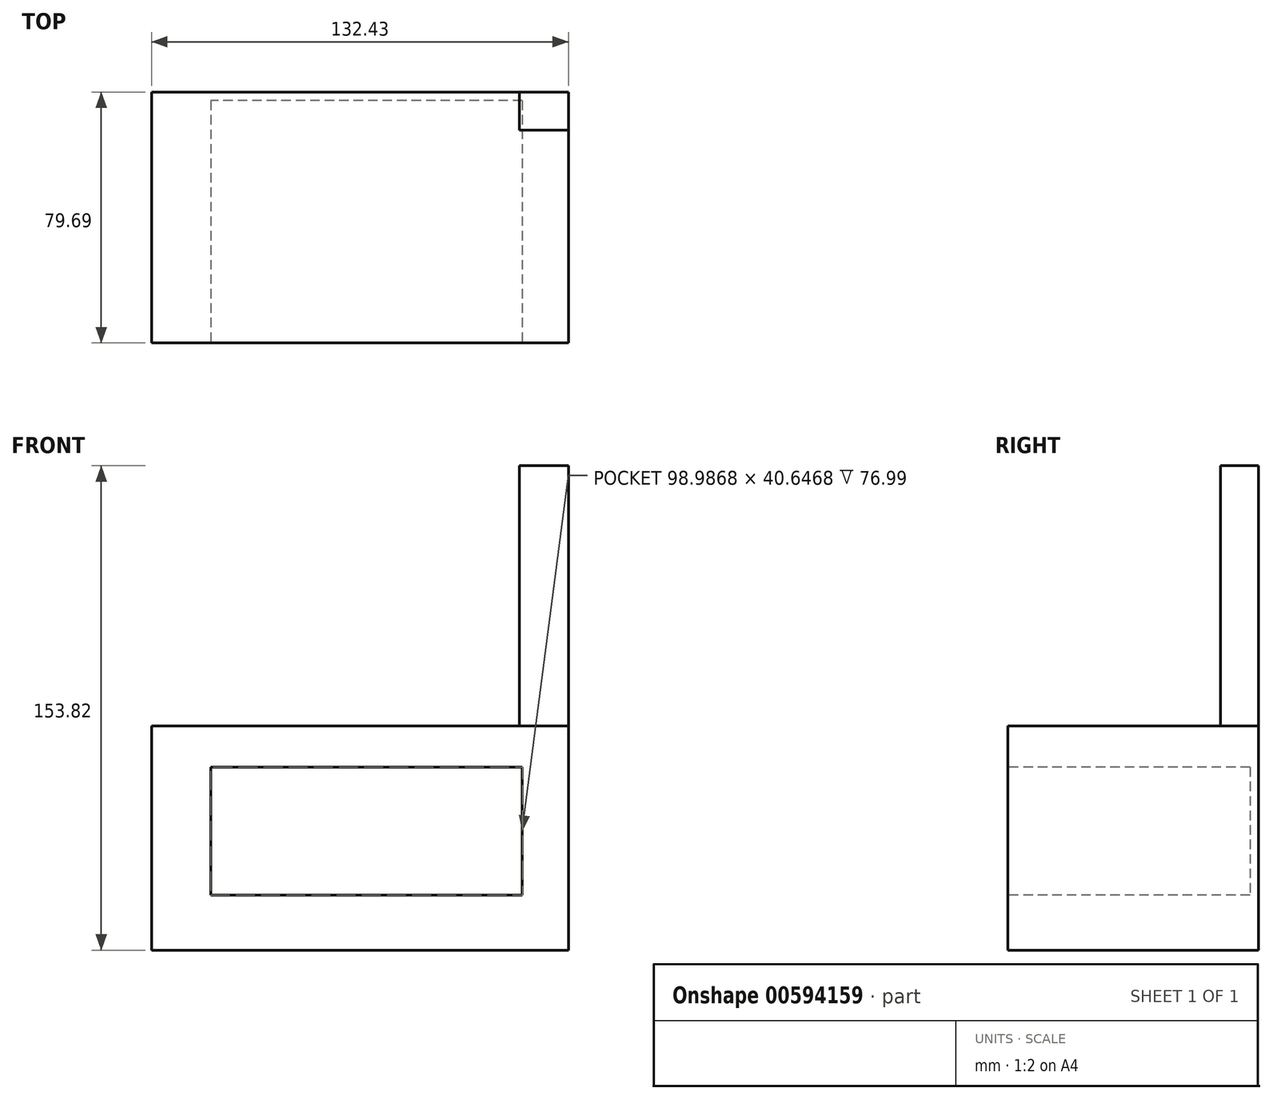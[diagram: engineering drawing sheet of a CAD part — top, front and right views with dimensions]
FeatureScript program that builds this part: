
annotation { "Feature Type Name" : "Feature", "Feature Type Description" : "" }
export const myFeature = defineFeature(function(context is Context, id is Id, definition is map)
    precondition{}
    {
        {
            var Q0;
            Q0=qCreatedBy(makeId("Top.planeOp"),FACE);
            var sketch = newSketch(context, id + "F0", { "sketchPlane" : qUnion([Q0])});
            skLineSegment(sketch, "E0.bottom", {"start": v(-68.33, -39.76) * mm, "end": v(64.1, -39.76) * mm});
            skLineSegment(sketch, "E0.top", {"start": v(-68.33, 39.93) * mm, "end": v(64.1, 39.93) * mm});
            skLineSegment(sketch, "E0.left", {"start": v(-68.33, -39.76) * mm, "end": v(-68.33, 39.93) * mm});
            skLineSegment(sketch, "E0.right", {"start": v(64.1, -39.76) * mm, "end": v(64.1, 39.93) * mm});
            skPoint(sketch, "E0.middle", {"position": v(-2.11, 0.09) * mm});
            skSolve(sketch);
        }
        {
            var Q0;
            Q0=makeQuery(id+"F0.imprint","IMPRINT",FACE,{"disambiguationData":[TD([[makeQuery(id+"F0.imprint","IMPRINT",EDGE,{"derivedFrom":sQuery(id+"F0.wireOp",EDGE,"E0.bottom")}),1.0]])]});
            extrude(context, id + "F1", {"entities" : qUnion([Q0]), "depth" : 71.13 * mm, "offsetDistance" : 25.4 * mm});
        }
        {
            var Q0;
            Q0=makeQuery(id+"F1.opExtrude","SWEPT_FACE",FACE,{"disambiguationData":[OSD([sQuery(id+"F0.wireOp",EDGE,"E0.bottom")])]});
            var sketch = newSketch(context, id + "F2", { "sketchPlane" : qUnion([Q0])});
            skLineSegment(sketch, "E1.bottom", {"start": v(49.5, 58.09) * mm, "end": v(-49.5, 58.09) * mm});
            skLineSegment(sketch, "E1.top", {"start": v(49.5, 17.44) * mm, "end": v(-49.5, 17.44) * mm});
            skLineSegment(sketch, "E1.left", {"start": v(49.5, 58.09) * mm, "end": v(49.5, 17.44) * mm});
            skLineSegment(sketch, "E1.right", {"start": v(-49.5, 58.09) * mm, "end": v(-49.5, 17.44) * mm});
            skPoint(sketch, "E1.middle", {"position": v(0, 37.76) * mm});
            skSolve(sketch);
        }
        {
            var Q0;
            Q0=makeQuery(id+"F2.imprint","IMPRINT",FACE,{"disambiguationData":[TD([[makeQuery(id+"F2.imprint","IMPRINT",EDGE,{"derivedFrom":sQuery(id+"F2.wireOp",EDGE,"E1.bottom")}),1.0]])]});
            var sketch = newSketch(context, id + "F3", { "sketchPlane" : qUnion([Q0])});
            skSolve(sketch);
        }
        {
            var Q0;
            Q0=makeQuery(id+"F3.imprint","IMPRINT",FACE,{"disambiguationData":[TD([[makeQuery(id+"F3.imprint","IMPRINT",EDGE,{"derivedFrom":makeQuery(id+"F2.imprint","IMPRINT",EDGE,{"derivedFrom":sQuery(id+"F2.wireOp",EDGE,"E1.bottom")})}),1.0]])]});
            extrude(context, id + "F4", {"entities" : qUnion([Q0]), "operationType" : NewBodyOperationType.REMOVE, "oppositeDirection" : true, "depth" : 77 * mm, "offsetDistance" : 25.4 * mm});
        }
        {
            var Q0;
            Q0=makeQuery(id+"F1.opExtrude","CAP_FACE",FACE,{"disambiguationData":[OSD([sQuery(id+"F0.wireOp",EDGE,"E0.bottom"),sQuery(id+"F0.wireOp",EDGE,"E0.top"),sQuery(id+"F0.wireOp",EDGE,"E0.left"),sQuery(id+"F0.wireOp",EDGE,"E0.right")])],"isStart":false});
            var sketch = newSketch(context, id + "F5", { "sketchPlane" : qUnion([Q0])});
            skLineSegment(sketch, "E2.bottom", {"start": v(64.1, 39.93) * mm, "end": v(48.5, 39.93) * mm});
            skLineSegment(sketch, "E2.top", {"start": v(64.1, 27.8) * mm, "end": v(48.5, 27.8) * mm});
            skLineSegment(sketch, "E2.left", {"start": v(64.1, 39.93) * mm, "end": v(64.1, 27.8) * mm});
            skLineSegment(sketch, "E2.right", {"start": v(48.5, 39.93) * mm, "end": v(48.5, 27.8) * mm});
            skSolve(sketch);
        }
        {
            var Q0;
            Q0=makeQuery(id+"F5.imprint","IMPRINT",FACE,{"disambiguationData":[TD([[makeQuery(id+"F5.imprint","IMPRINT",EDGE,{"derivedFrom":sQuery(id+"F5.wireOp",EDGE,"E2.bottom")}),-1.0]])]});
            extrude(context, id + "F6", {"entities" : qUnion([Q0]), "depth" : 82.68 * mm, "offsetDistance" : 25.4 * mm});
        }
    });
